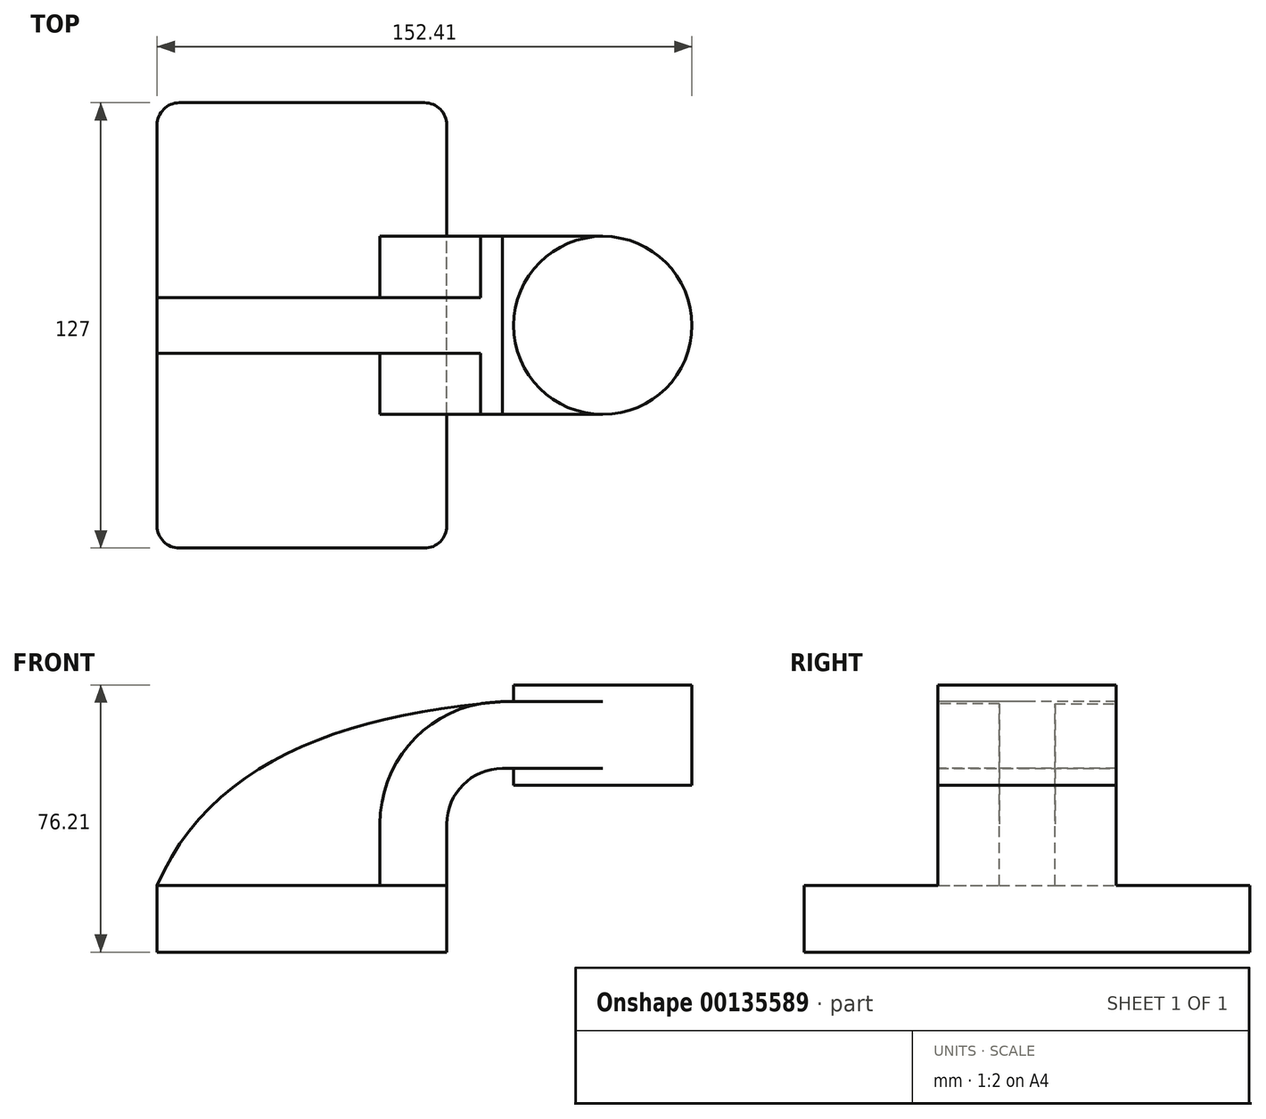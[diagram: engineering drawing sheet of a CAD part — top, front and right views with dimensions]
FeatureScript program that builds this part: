
annotation { "Feature Type Name" : "Feature", "Feature Type Description" : "" }
export const myFeature = defineFeature(function(context is Context, id is Id, definition is map)
    precondition{}
    {
        {
            var Q0;
            Q0=qCreatedBy(makeId("Front.planeOp"),FACE);
            var sketch = newSketch(context, id + "F0", { "sketchPlane" : qUnion([Q0])});
            skLineSegment(sketch, "E0.bottom", {"start": v(41.27, 9.53) * mm, "end": v(-41.28, 9.53) * mm});
            skLineSegment(sketch, "E0.top", {"start": v(41.28, -9.52) * mm, "end": v(-41.27, -9.52) * mm});
            skLineSegment(sketch, "E0.left", {"start": v(41.28, 9.53) * mm, "end": v(41.28, -9.52) * mm});
            skLineSegment(sketch, "E0.right", {"start": v(-41.28, 9.53) * mm, "end": v(-41.27, -9.52) * mm});
            skPoint(sketch, "E0.middle", {"position": v(0, 0) * mm});
            skLineSegment(sketch, "E1.bottom", {"start": v(60.32, 66.68) * mm, "end": v(111.12, 66.68) * mm});
            skLineSegment(sketch, "E1.top", {"start": v(60.32, 38.1) * mm, "end": v(111.12, 38.1) * mm});
            skLineSegment(sketch, "E1.left", {"start": v(60.32, 66.68) * mm, "end": v(60.32, 38.1) * mm});
            skLineSegment(sketch, "E1.right", {"start": v(111.12, 66.68) * mm, "end": v(111.12, 38.1) * mm});
            skPoint(sketch, "E1.middle", {"position": v(85.72, 52.39) * mm});
            skLineSegment(sketch, "E2", {"start": v(41.27, 9.53) * mm, "end": v(41.27, 26.99) * mm});
            skArc(sketch, "E3", {"start": v(41.27, 26.99) * mm, "mid": v(45.92, 38.21) * mm, "end": v(57.15, 42.86) * mm});
            skLineSegment(sketch, "E4", {"start": v(57.15, 42.86) * mm, "end": v(85.72, 42.86) * mm});
            skLineSegment(sketch, "E5.0", {"start": v(57.15, 61.91) * mm, "end": v(85.72, 61.91) * mm});
            skArc(sketch, "E5.1", {"start": v(22.23, 26.99) * mm, "mid": v(32.45, 51.68) * mm, "end": v(57.15, 61.91) * mm});
            skLineSegment(sketch, "E5.2", {"start": v(22.22, 9.53) * mm, "end": v(22.22, 26.99) * mm});
            skLineSegment(sketch, "E6", {"start": v(85.72, 38.1) * mm, "end": v(85.72, 66.68) * mm});
            skFitSpline(sketch, "E7", {"points": [v(-41.28, 9.53) * mm, v(57.15, 61.91) * mm], "startDerivative": vector(43.92, 102.5) * mm, "endDerivative": vector(140.65, 11.08) * mm});
            skSolve(sketch);
        }
        {
            var Q0;
            Q0=makeQuery(id+"F0.imprint","IMPRINT",FACE,{"disambiguationData":[TD([[makeQuery(id+"F0.imprint","IMPRINT",EDGE,{"derivedFrom":sQuery(id+"F0.wireOp",EDGE,"E0.top")}),-1.0]])]});
            extrude(context, id + "F1", {"entities" : qUnion([Q0]), "endBound" : BoundingType.SYMMETRIC, "depth" : 127 * mm});
        }
        {
            var Q0;
            {var subQ1=sQuery(id+"F0.wireOp",EDGE,"E2");Q0=makeQuery(id+"F0.imprint","IMPRINT",FACE,{"disambiguationData":[TD([[makeQuery(id+"F0.imprint","IMPRINT",EDGE,{"derivedFrom":subQ1}),1.0]])]});}
            var Q1;
            {var subQ0=sQuery(id+"F0.wireOp",EDGE,"E5.0");var subQ1=sQuery(id+"F0.wireOp",EDGE,"E1.left");var subQ2=makeQuery(id+"F0.imprint","INTERSECT",VERTEX,{"derivedFrom":[subQ1,subQ0]});Q1=makeQuery(id+"F0.imprint","IMPRINT",FACE,{"disambiguationData":[TD([[makeQuery(id+"F0.imprint","IMPRINT",EDGE,{"disambiguationData":[TD([[subQ2,-1.0]])],"derivedFrom":subQ1}),1.0]])]});}
            extrude(context, id + "F2", {"entities" : qUnion([Q0, Q1]), "operationType" : NewBodyOperationType.ADD, "endBound" : BoundingType.SYMMETRIC, "depth" : 50.8 * mm});
        }
        {
            var Q0;
            {var subQ3=sQuery(id+"F0.wireOp",EDGE,"E5.2");Q0=makeQuery(id+"F0.imprint","IMPRINT",FACE,{"disambiguationData":[TD([[makeQuery(id+"F0.imprint","IMPRINT",EDGE,{"derivedFrom":subQ3}),1.0]])]});}
            extrude(context, id + "F3", {"entities" : qUnion([Q0]), "operationType" : NewBodyOperationType.ADD, "endBound" : BoundingType.SYMMETRIC, "depth" : 15.88 * mm});
        }
        {
            var Q0;
            {var subQ0=sQuery(id+"F0.wireOp",EDGE,"E1.right");Q0=makeQuery(id+"F0.imprint","IMPRINT",FACE,{"disambiguationData":[TD([[makeQuery(id+"F0.imprint","IMPRINT",EDGE,{"derivedFrom":subQ0}),-1.0]])]});}
            var Q1;
            Q1=sQuery(id+"F0.wireOp",EDGE,"E6");
            revolve(context, id + "F4", {"operationType" : NewBodyOperationType.ADD, "entities" : qUnion([Q0]), "axis" : qUnion([Q1]), "revolveType" : RevolveType.FULL});
        }
        {
            var Q0;
            Q0=makeQuery(id+"F1.opExtrude","CAP_EDGE",EDGE,{"disambiguationData":[OSD([sQuery(id+"F0.wireOp",EDGE,"E0.left")])],"isStart":true});
            var Q1;
            Q1=makeQuery(id+"F1.opExtrude","CAP_EDGE",EDGE,{"disambiguationData":[OSD([sQuery(id+"F0.wireOp",EDGE,"E0.left")])],"isStart":false});
            var Q2;
            Q2=makeQuery(id+"F1.opExtrude","CAP_EDGE",EDGE,{"disambiguationData":[OSD([sQuery(id+"F0.wireOp",EDGE,"E0.right")])],"isStart":false});
            var Q3;
            Q3=makeQuery(id+"F1.opExtrude","CAP_EDGE",EDGE,{"disambiguationData":[OSD([sQuery(id+"F0.wireOp",EDGE,"E0.right")])],"isStart":true});
            fillet(context, id + "F5", {"entities" : qUnion([Q0, Q1, Q2, Q3]), "radius" : 6.35 * mm, "tangentPropagation" : true, "allowEdgeOverflow" : false});
        }
    });
